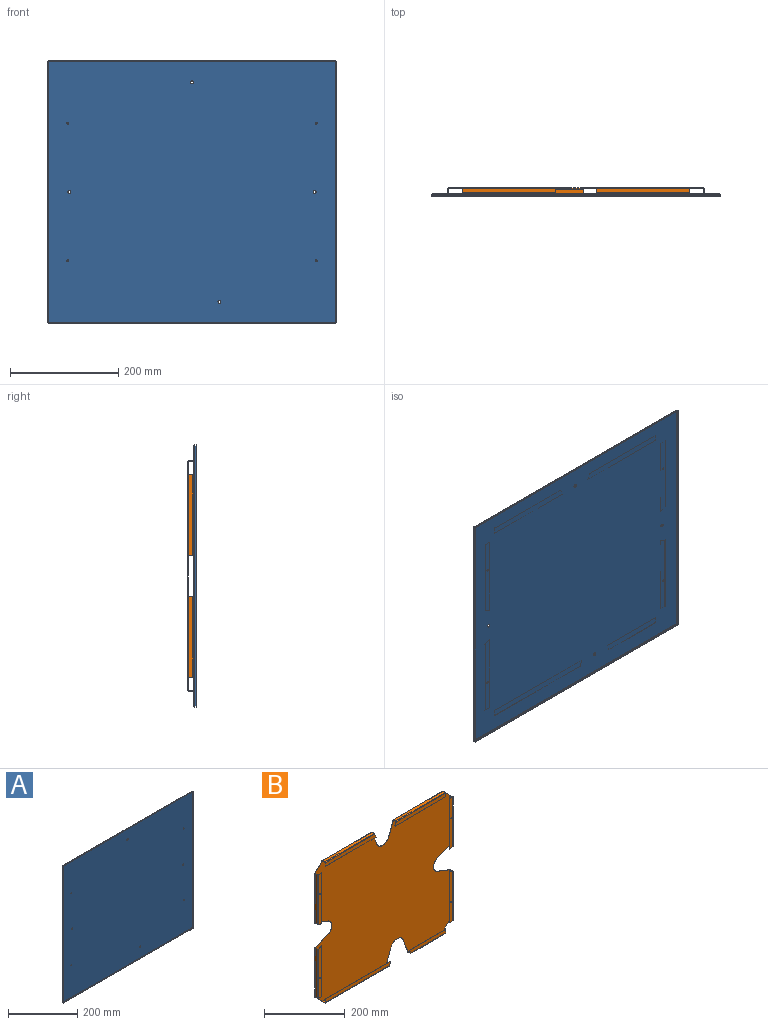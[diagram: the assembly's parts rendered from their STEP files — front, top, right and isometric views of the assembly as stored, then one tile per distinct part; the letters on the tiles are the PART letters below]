
ASSEMBLY  parts=2 mates=1
PART A: 46 faces, bbox 532.5x4x485.5 mm
  f0: plane 529.09x0.86mm, normal (0,-1,0), area 456.9mm2, adj f1,f2,f3,f4
  f1: plane 2.31x0.86mm, normal (1,0,0), area 2mm2, adj f0,f3,f4,f43
  f2: plane 2.31x0.86mm, normal (-1,0,0), area 2mm2, adj f0,f3,f4,f42
  f3: plane 529.09x2.31mm, normal (0,0,1), area 1222.9mm2, adj f0,f1,f2,f44
  f4: plane 529.09x2.31mm, normal (0,0,-1), area 1222.9mm2, adj f0,f1,f2,f45
  f5: cylinder r=1.63mm len=3.26mm, axis (0,-1,0), area 8.9mm2, adj f13,f14
  f6: cylinder r=1.63mm len=3.26mm, axis (0,-1,0), area 8.9mm2, adj f13,f14
  f7: cylinder r=1.63mm len=3.26mm, axis (0,-1,0), area 8.9mm2, adj f13,f14
  f8: cylinder r=1.63mm len=3.26mm, axis (0,-1,0), area 8.9mm2, adj f13,f14
  f9: cylinder r=2.77mm len=5.54mm, axis (0,-1,0), area 15mm2, adj f13,f14
  f10: cylinder r=2.77mm len=5.54mm, axis (0,-1,0), area 15mm2, adj f13,f14
  f11: cylinder r=2.77mm len=5.54mm, axis (0,-1,0), area 15mm2, adj f13,f14
  f12: cylinder r=2.77mm len=5.54mm, axis (0,-1,0), area 15mm2, adj f13,f14
  f13: plane 529.09x482.04mm, normal (0,1,0), area 254915.7mm2, adj f5,f6,f7,f8,f9,f10,f11,f12
  f14: plane 529.09x482.04mm, normal (0,-1,0), area 254915.7mm2, adj f5,f6,f7,f8,f9,f10,f11,f12
  f15: plane 529.09x0.86mm, normal (0,-1,0), area 456.9mm2, adj f16,f17,f18,f19
  f16: plane 2.31x0.86mm, normal (-1,0,0), area 2mm2, adj f15,f18,f19,f20
  f17: plane 2.31x0.86mm, normal (1,0,0), area 2mm2, adj f15,f18,f19,f21
  f18: plane 529.09x2.31mm, normal (0,0,-1), area 1222.9mm2, adj f15,f16,f17,f22
  f19: plane 529.09x2.31mm, normal (0,0,1), area 1222.9mm2, adj f15,f16,f17,f23
  f20: plane 1.73x1.73mm, normal (-1,0,0), area 1.8mm2, adj f16,f22,f23,f38
  f21: plane 1.73x1.73mm, normal (1,0,0), area 1.8mm2, adj f17,f22,f23,f29
  f22: cylinder r=1.73mm len=529.09mm, axis (-1,0,0), area 1435.5mm2, adj f13,f18,f20,f21
  f23: cylinder r=0.86mm len=529.09mm, axis (-1,0,0), area 717.7mm2, adj f14,f19,f20,f21
  f24: plane 482.04x0.86mm, normal (0,-1,0), area 416.3mm2, adj f25,f26,f27,f28
  f25: plane 2.31x0.86mm, normal (0,0,-1), area 2mm2, adj f24,f27,f28,f29
  f26: plane 2.31x0.86mm, normal (0,0,1), area 2mm2, adj f24,f27,f28,f30
  f27: plane 482.04x2.31mm, normal (1,0,0), area 1114.2mm2, adj f24,f25,f26,f31
  f28: plane 482.04x2.31mm, normal (-1,0,0), area 1114.2mm2, adj f24,f25,f26,f32
  f29: plane 1.73x1.73mm, normal (0,0,-1), area 1.8mm2, adj f21,f25,f31,f32
  f30: plane 1.73x1.73mm, normal (0,0,1), area 1.8mm2, adj f26,f31,f32,f43
  f31: cylinder r=1.73mm len=482.04mm, axis (0,0,-1), area 1307.8mm2, adj f13,f27,f29,f30
  f32: cylinder r=0.86mm len=482.04mm, axis (0,0,-1), area 653.9mm2, adj f14,f28,f29,f30
  f33: plane 482.04x0.86mm, normal (0,-1,0), area 416.3mm2, adj f34,f35,f36,f37
  f34: plane 2.31x0.86mm, normal (0,0,1), area 2mm2, adj f33,f36,f37,f39
  f35: plane 2.31x0.86mm, normal (0,0,-1), area 2mm2, adj f33,f36,f37,f38
  f36: plane 482.04x2.31mm, normal (-1,0,0), area 1114.2mm2, adj f33,f34,f35,f40
  f37: plane 482.04x2.31mm, normal (1,0,0), area 1114.2mm2, adj f33,f34,f35,f41
  f38: plane 1.73x1.73mm, normal (0,0,-1), area 1.8mm2, adj f20,f35,f40,f41
  f39: plane 1.73x1.73mm, normal (0,0,1), area 1.8mm2, adj f34,f40,f41,f42
  f40: cylinder r=1.73mm len=482.04mm, axis (0,0,-1), area 1307.8mm2, adj f13,f36,f38,f39
  f41: cylinder r=0.86mm len=482.04mm, axis (0,0,-1), area 653.9mm2, adj f14,f37,f38,f39
  f42: plane 1.73x1.73mm, normal (-1,0,0), area 1.8mm2, adj f2,f39,f44,f45
  f43: plane 1.73x1.73mm, normal (1,0,0), area 1.8mm2, adj f1,f30,f44,f45
  f44: cylinder r=1.73mm len=529.09mm, axis (-1,0,0), area 1435.5mm2, adj f3,f13,f42,f43
  f45: cylinder r=0.86mm len=529.09mm, axis (-1,0,0), area 717.7mm2, adj f4,f14,f42,f43
PART B: 158 faces, bbox 473.7x11.1x426.6 mm
  f0: plane 43.46x16.69mm, normal (-0.93,0,-0.36), area 40.2mm2, adj f1,f16,f17,f31
  f1: cylinder r=22.23mm len=41.5mm, axis (0,-1,0), area 46.2mm2, adj f0,f2,f16,f17
  f2: plane 43.46x16.69mm, normal (0.93,0,-0.36), area 40.2mm2, adj f1,f16,f17,f70
  f3: plane 23.67x23.67mm, normal (-0.71,0,-0.71), area 28.9mm2, adj f16,f17,f69,f154
  f4: plane 43.46x16.69mm, normal (-0.36,0,0.93), area 40.2mm2, adj f5,f16,f17,f155
  f5: cylinder r=22.23mm len=41.5mm, axis (0,-1,0), area 46.2mm2, adj f4,f6,f16,f17
  f6: plane 43.46x16.69mm, normal (-0.36,0,-0.93), area 40.2mm2, adj f5,f16,f17,f136
  f7: plane 23.67x23.67mm, normal (-0.71,0,0.71), area 28.9mm2, adj f16,f17,f52,f137
  f8: plane 43.46x16.69mm, normal (0.93,0,0.36), area 40.2mm2, adj f9,f16,f17,f53
  f9: cylinder r=22.23mm len=41.5mm, axis (0,-1,0), area 46.2mm2, adj f8,f10,f16,f17
  f10: plane 43.46x16.69mm, normal (-0.93,0,0.36), area 40.2mm2, adj f9,f16,f17,f48
  f11: plane 23.67x23.67mm, normal (0.71,0,0.71), area 28.9mm2, adj f16,f17,f49,f119
  f12: plane 43.46x16.69mm, normal (0.36,0,-0.93), area 40.2mm2, adj f13,f16,f17,f118
  f13: cylinder r=22.23mm len=41.5mm, axis (0,-1,0), area 46.2mm2, adj f12,f14,f16,f17
  f14: plane 43.46x16.69mm, normal (0.36,0,0.93), area 40.2mm2, adj f13,f16,f17,f101
  f15: plane 23.67x23.67mm, normal (0.71,0,-0.71), area 28.9mm2, adj f16,f17,f32,f100
  f16: plane 470.22x423.16mm, normal (0,1,0), area 186026.2mm2, adj f0,f1,f2,f3,f4,f5,f6,f7
  f17: plane 470.22x423.16mm, normal (0,-1,0), area 186026.2mm2, adj f0,f1,f2,f3,f4,f5,f6,f7
  f18: plane 7.66x0.86mm, normal (1,0,0), area 6.6mm2, adj f20,f21,f28,f32
  f19: plane 7.66x0.86mm, normal (-1,0,0), area 6.6mm2, adj f20,f21,f27,f31
  f20: plane 122.32x7.66mm, normal (0,0,-1), area 936.7mm2, adj f18,f19,f29,f33
  f21: plane 122.32x7.66mm, normal (0,0,1), area 936.7mm2, adj f18,f19,f30,f34
  f22: plane 10.97x0.86mm, normal (1,0,0), area 9.5mm2, adj f23,f25,f26,f28
  f23: plane 126.55x0.86mm, normal (0,0,1), area 109.3mm2, adj f22,f24,f25,f26
  f24: plane 10.97x4.21mm, normal (-0.93,0,-0.36), area 10.2mm2, adj f23,f25,f26,f27
  f25: plane 126.55x10.97mm, normal (0,-1,0), area 1365.5mm2, adj f22,f23,f24,f29
  f26: plane 126.55x10.97mm, normal (0,1,0), area 1365.5mm2, adj f22,f23,f24,f30
  f27: bspline ~1.73x1.73mm, area 1.8mm2, adj f19,f24,f29,f30
  f28: plane 1.73x1.73mm, normal (1,0,0), area 1.8mm2, adj f18,f22,f29,f30
  f29: cylinder r=1.73mm len=122.34mm, axis (-1,0,0), area 331.9mm2, adj f20,f25,f27,f28
  f30: cylinder r=0.86mm len=122.34mm, axis (-1,0,0), area 165.9mm2, adj f21,f26,f27,f28
  f31: bspline ~1.73x1.73mm, area 1.8mm2, adj f0,f19,f33,f34
  f32: bspline ~1.73x1.73mm, area 2mm2, adj f15,f18,f33,f34
  f33: cylinder r=1.73mm len=123.2mm, axis (-1,0,0), area 332.5mm2, adj f16,f20,f31,f32
  f34: cylinder r=0.86mm len=123.2mm, axis (-1,0,0), area 166.2mm2, adj f17,f21,f31,f32
  f35: plane 177.35x0.86mm, normal (0,0,-1), area 153.2mm2, adj f36,f37,f38,f39
  f36: plane 10.97x0.86mm, normal (1,0,0), area 9.5mm2, adj f35,f38,f39,f41
  f37: plane 10.97x4.21mm, normal (-0.93,0,0.36), area 10.2mm2, adj f35,f38,f39,f40
  f38: plane 177.35x10.97mm, normal (0,-1,0), area 1922.9mm2, adj f35,f36,f37,f42
  f39: plane 177.35x10.97mm, normal (0,1,0), area 1922.9mm2, adj f35,f36,f37,f43
  f40: bspline ~1.73x1.73mm, area 1.8mm2, adj f37,f42,f43,f45
  f41: plane 1.73x1.73mm, normal (1,0,0), area 1.8mm2, adj f36,f42,f43,f44
  f42: cylinder r=1.73mm len=173.14mm, axis (-1,0,0), area 469.7mm2, adj f38,f40,f41,f46
  f43: cylinder r=0.86mm len=173.14mm, axis (-1,0,0), area 234.9mm2, adj f39,f40,f41,f47
  f44: plane 7.66x0.86mm, normal (1,0,0), area 6.6mm2, adj f41,f46,f47,f49
  f45: plane 7.66x0.86mm, normal (-1,0,0), area 6.6mm2, adj f40,f46,f47,f48
  f46: plane 173.12x7.66mm, normal (0,0,1), area 1325.8mm2, adj f42,f44,f45,f50
  f47: plane 173.12x7.66mm, normal (0,0,-1), area 1325.8mm2, adj f43,f44,f45,f51
  f48: bspline ~1.73x1.73mm, area 1.8mm2, adj f10,f45,f50,f51
  f49: bspline ~1.73x1.73mm, area 2mm2, adj f11,f44,f50,f51
  f50: cylinder r=1.73mm len=174mm, axis (-1,0,0), area 470.3mm2, adj f16,f46,f48,f49
  f51: cylinder r=0.86mm len=174mm, axis (-1,0,0), area 235.1mm2, adj f17,f47,f48,f49
  f52: bspline ~1.73x1.73mm, area 2mm2, adj f7,f54,f55,f73
  f53: bspline ~1.73x1.73mm, area 1.8mm2, adj f8,f54,f55,f74
  f54: cylinder r=1.73mm len=174mm, axis (-1,0,0), area 470.3mm2, adj f16,f52,f53,f75
  f55: cylinder r=0.86mm len=174mm, axis (-1,0,0), area 235.2mm2, adj f17,f52,f53,f76
  f56: plane 228.15x0.86mm, normal (0,0,1), area 197mm2, adj f57,f58,f59,f60
  f57: plane 10.97x0.86mm, normal (-1,0,0), area 9.5mm2, adj f56,f59,f60,f61
  f58: plane 10.97x4.21mm, normal (0.93,0,-0.36), area 10.2mm2, adj f56,f59,f60,f62
  f59: plane 228.15x10.97mm, normal (0,-1,0), area 2480.3mm2, adj f56,f57,f58,f63
  f60: plane 228.15x10.97mm, normal (0,1,0), area 2480.3mm2, adj f56,f57,f58,f64
  f61: plane 1.73x1.73mm, normal (-1,0,0), area 1.8mm2, adj f57,f63,f64,f65
  f62: bspline ~1.73x1.73mm, area 1.8mm2, adj f58,f63,f64,f66
  f63: cylinder r=1.73mm len=223.94mm, axis (-1,0,0), area 607.5mm2, adj f59,f61,f62,f67
  f64: cylinder r=0.86mm len=223.94mm, axis (-1,0,0), area 303.8mm2, adj f60,f61,f62,f68
  f65: plane 7.66x0.86mm, normal (-1,0,0), area 6.6mm2, adj f61,f67,f68,f69
  f66: plane 7.66x0.86mm, normal (1,0,0), area 6.6mm2, adj f62,f67,f68,f70
  f67: plane 223.92x7.66mm, normal (0,0,-1), area 1714.8mm2, adj f63,f65,f66,f71
  f68: plane 223.92x7.66mm, normal (0,0,1), area 1714.8mm2, adj f64,f65,f66,f72
  f69: bspline ~1.73x1.73mm, area 2mm2, adj f3,f65,f71,f72
  f70: bspline ~1.73x1.73mm, area 1.8mm2, adj f2,f66,f71,f72
  f71: cylinder r=1.73mm len=224.8mm, axis (-1,0,0), area 608.1mm2, adj f16,f67,f69,f70
  f72: cylinder r=0.86mm len=224.8mm, axis (-1,0,0), area 304.1mm2, adj f17,f68,f69,f70
  f73: plane 7.66x0.86mm, normal (-1,0,0), area 6.6mm2, adj f52,f75,f76,f82
  f74: plane 7.66x0.86mm, normal (1,0,0), area 6.6mm2, adj f53,f75,f76,f83
  f75: plane 173.12x7.66mm, normal (0,0,1), area 1325.8mm2, adj f54,f73,f74,f84
  f76: plane 173.12x7.66mm, normal (0,0,-1), area 1325.8mm2, adj f55,f73,f74,f85
  f77: plane 10.97x0.86mm, normal (-1,0,0), area 9.5mm2, adj f78,f80,f81,f82
  f78: plane 177.35x0.86mm, normal (0,0,-1), area 153.2mm2, adj f77,f79,f80,f81
  f79: plane 10.97x4.21mm, normal (0.93,0,0.36), area 10.2mm2, adj f78,f80,f81,f83
  f80: plane 177.35x10.97mm, normal (0,-1,0), area 1922.9mm2, adj f77,f78,f79,f84
  f81: plane 177.35x10.97mm, normal (0,1,0), area 1922.9mm2, adj f77,f78,f79,f85
  f82: plane 1.73x1.73mm, normal (-1,0,0), area 1.8mm2, adj f73,f77,f84,f85
  f83: bspline ~1.73x1.73mm, area 1.8mm2, adj f74,f79,f84,f85
  f84: cylinder r=1.73mm len=173.14mm, axis (-1,0,0), area 469.7mm2, adj f75,f80,f82,f83
  f85: cylinder r=0.86mm len=173.14mm, axis (-1,0,0), area 234.9mm2, adj f76,f81,f82,f83
  f86: plane 153.82x0.86mm, normal (-1,0,0), area 132.8mm2, adj f87,f89,f90,f91
  f87: plane 10.97x0.86mm, normal (0,0,-1), area 9.5mm2, adj f86,f90,f91,f92
  f88: cylinder r=1.63mm len=3.26mm, axis (0,-1,0), area 8.9mm2, adj f90,f91
  f89: plane 10.97x4.21mm, normal (0.36,0,0.93), area 10.2mm2, adj f86,f90,f91,f93
  f90: plane 153.82x10.97mm, normal (0,-1,0), area 1656.4mm2, adj f86,f87,f88,f89,f94
  f91: plane 153.82x10.97mm, normal (0,1,0), area 1656.4mm2, adj f86,f87,f88,f89,f95
  f92: plane 1.73x1.73mm, normal (0,0,-1), area 1.8mm2, adj f87,f94,f95,f96
  f93: bspline ~1.73x1.73mm, area 1.8mm2, adj f89,f94,f95,f97
  f94: cylinder r=1.73mm len=149.61mm, axis (0,0,-1), area 405.9mm2, adj f90,f92,f93,f98
  f95: cylinder r=0.86mm len=149.61mm, axis (0,0,-1), area 202.9mm2, adj f91,f92,f93,f99
  f96: plane 7.66x0.86mm, normal (0,0,-1), area 6.6mm2, adj f92,f98,f99,f100
  f97: plane 7.66x0.86mm, normal (0,0,1), area 6.6mm2, adj f93,f98,f99,f101
  f98: plane 149.59x7.66mm, normal (1,0,0), area 1145.6mm2, adj f94,f96,f97,f102
  f99: plane 149.59x7.66mm, normal (-1,0,0), area 1145.6mm2, adj f95,f96,f97,f103
  f100: bspline ~1.73x1.73mm, area 2mm2, adj f15,f96,f102,f103
  f101: bspline ~1.73x1.73mm, area 1.8mm2, adj f14,f97,f102,f103
  f102: cylinder r=1.73mm len=150.47mm, axis (0,0,-1), area 406.5mm2, adj f16,f98,f100,f101
  f103: cylinder r=0.86mm len=150.47mm, axis (0,0,-1), area 203.2mm2, adj f17,f99,f100,f101
  f104: plane 10.97x0.86mm, normal (0,0,1), area 9.5mm2, adj f105,f108,f109,f111
  f105: plane 153.82x0.86mm, normal (-1,0,0), area 132.8mm2, adj f104,f106,f108,f109
  f106: plane 10.97x4.21mm, normal (0.36,0,-0.93), area 10.2mm2, adj f105,f108,f109,f110
  f107: cylinder r=1.63mm len=3.26mm, axis (0,-1,0), area 8.9mm2, adj f108,f109
  f108: plane 153.82x10.97mm, normal (0,-1,0), area 1656.4mm2, adj f104,f105,f106,f107,f112
  f109: plane 153.82x10.97mm, normal (0,1,0), area 1656.4mm2, adj f104,f105,f106,f107,f113
  f110: bspline ~1.73x1.73mm, area 1.8mm2, adj f106,f112,f113,f115
  f111: plane 1.73x1.73mm, normal (0,0,1), area 1.8mm2, adj f104,f112,f113,f114
  f112: cylinder r=1.73mm len=149.61mm, axis (0,0,-1), area 405.9mm2, adj f108,f110,f111,f116
  f113: cylinder r=0.86mm len=149.61mm, axis (0,0,-1), area 202.9mm2, adj f109,f110,f111,f117
  f114: plane 7.66x0.86mm, normal (0,0,1), area 6.6mm2, adj f111,f116,f117,f119
  f115: plane 7.66x0.86mm, normal (0,0,-1), area 6.6mm2, adj f110,f116,f117,f118
  f116: plane 149.59x7.66mm, normal (1,0,0), area 1145.6mm2, adj f112,f114,f115,f120
  f117: plane 149.59x7.66mm, normal (-1,0,0), area 1145.6mm2, adj f113,f114,f115,f121
  f118: bspline ~1.73x1.73mm, area 1.8mm2, adj f12,f115,f120,f121
  f119: bspline ~1.73x1.73mm, area 2mm2, adj f11,f114,f120,f121
  f120: cylinder r=1.73mm len=150.47mm, axis (0,0,-1), area 406.5mm2, adj f16,f116,f118,f119
  f121: cylinder r=0.86mm len=150.47mm, axis (0,0,-1), area 203.2mm2, adj f17,f117,f118,f119
  f122: plane 153.82x0.86mm, normal (1,0,0), area 132.8mm2, adj f123,f125,f126,f127
  f123: plane 10.97x0.86mm, normal (0,0,1), area 9.5mm2, adj f122,f126,f127,f129
  f124: cylinder r=1.63mm len=3.26mm, axis (0,-1,0), area 8.9mm2, adj f126,f127
  f125: plane 10.97x4.21mm, normal (-0.36,0,-0.93), area 10.2mm2, adj f122,f126,f127,f128
  f126: plane 153.82x10.97mm, normal (0,-1,0), area 1656.4mm2, adj f122,f123,f124,f125,f130
  f127: plane 153.82x10.97mm, normal (0,1,0), area 1656.4mm2, adj f122,f123,f124,f125,f131
  f128: bspline ~1.73x1.73mm, area 1.8mm2, adj f125,f130,f131,f133
  f129: plane 1.73x1.73mm, normal (0,0,1), area 1.8mm2, adj f123,f130,f131,f132
  f130: cylinder r=1.73mm len=149.61mm, axis (0,0,-1), area 405.9mm2, adj f126,f128,f129,f134
  f131: cylinder r=0.86mm len=149.61mm, axis (0,0,-1), area 202.9mm2, adj f127,f128,f129,f135
  f132: plane 7.66x0.86mm, normal (0,0,1), area 6.6mm2, adj f129,f134,f135,f137
  f133: plane 7.66x0.86mm, normal (0,0,-1), area 6.6mm2, adj f128,f134,f135,f136
  f134: plane 149.59x7.66mm, normal (-1,0,0), area 1145.6mm2, adj f130,f132,f133,f138
  f135: plane 149.59x7.66mm, normal (1,0,0), area 1145.6mm2, adj f131,f132,f133,f139
  f136: bspline ~1.73x1.73mm, area 1.8mm2, adj f6,f133,f138,f139
  f137: bspline ~1.73x1.73mm, area 2mm2, adj f7,f132,f138,f139
  f138: cylinder r=1.73mm len=150.47mm, axis (0,0,-1), area 406.5mm2, adj f16,f134,f136,f137
  f139: cylinder r=0.86mm len=150.47mm, axis (0,0,-1), area 203.2mm2, adj f17,f135,f136,f137
  f140: plane 10.97x0.86mm, normal (0,0,-1), area 9.5mm2, adj f141,f144,f145,f146
  f141: plane 153.82x0.86mm, normal (1,0,0), area 132.8mm2, adj f140,f142,f144,f145
  f142: plane 10.97x4.21mm, normal (-0.36,0,0.93), area 10.2mm2, adj f141,f144,f145,f147
  f143: cylinder r=1.63mm len=3.26mm, axis (0,-1,0), area 8.9mm2, adj f144,f145
  f144: plane 153.82x10.97mm, normal (0,-1,0), area 1656.4mm2, adj f140,f141,f142,f143,f148
  f145: plane 153.82x10.97mm, normal (0,1,0), area 1656.4mm2, adj f140,f141,f142,f143,f149
  f146: plane 1.73x1.73mm, normal (0,0,-1), area 1.8mm2, adj f140,f148,f149,f150
  f147: bspline ~1.73x1.73mm, area 1.8mm2, adj f142,f148,f149,f151
  f148: cylinder r=1.73mm len=149.61mm, axis (0,0,-1), area 405.9mm2, adj f144,f146,f147,f152
  f149: cylinder r=0.86mm len=149.61mm, axis (0,0,-1), area 202.9mm2, adj f145,f146,f147,f153
  f150: plane 7.66x0.86mm, normal (0,0,-1), area 6.6mm2, adj f146,f152,f153,f154
  f151: plane 7.66x0.86mm, normal (0,0,1), area 6.6mm2, adj f147,f152,f153,f155
  f152: plane 149.59x7.66mm, normal (-1,0,0), area 1145.6mm2, adj f148,f150,f151,f156
  f153: plane 149.59x7.66mm, normal (1,0,0), area 1145.6mm2, adj f149,f150,f151,f157
  f154: bspline ~1.73x1.73mm, area 2mm2, adj f3,f150,f156,f157
  f155: bspline ~1.73x1.73mm, area 1.8mm2, adj f4,f151,f156,f157
  f156: cylinder r=1.73mm len=150.47mm, axis (0,0,-1), area 406.5mm2, adj f16,f152,f154,f155
  f157: cylinder r=0.86mm len=150.47mm, axis (0,0,-1), area 203.2mm2, adj f17,f153,f154,f155
PLACE A at identity fixed
PLACE B t=(0,6.42,0)mm
MATE fastened B.f124 <-> A.f8  axis (0,-1,0) through (-229.62,0.86,127)mm
